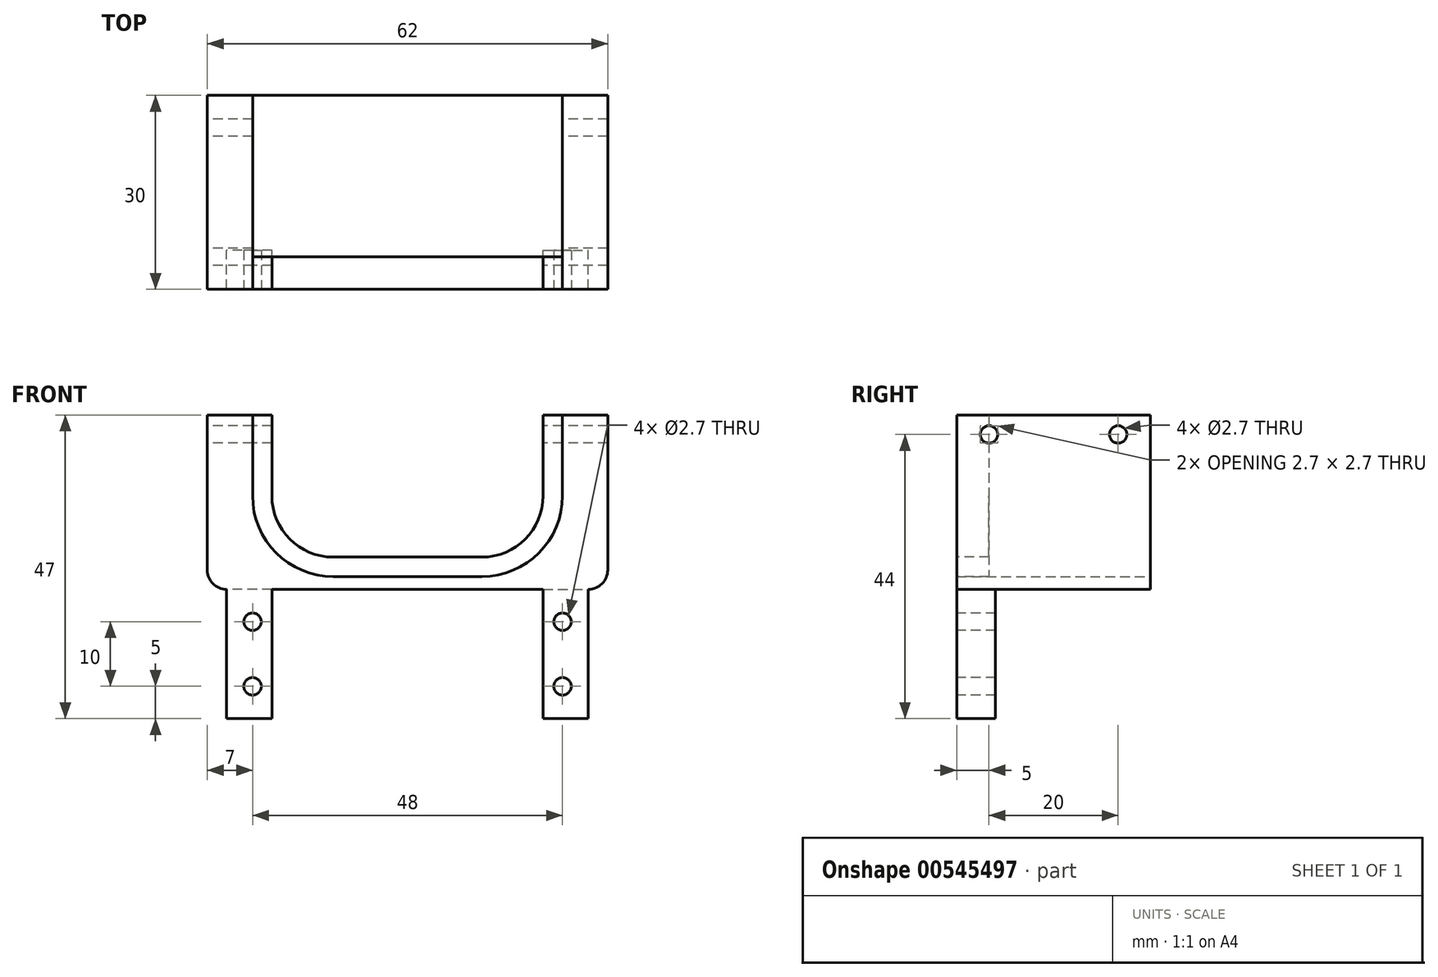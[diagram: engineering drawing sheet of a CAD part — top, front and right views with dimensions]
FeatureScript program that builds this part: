
annotation { "Feature Type Name" : "Feature", "Feature Type Description" : "" }
export const myFeature = defineFeature(function(context is Context, id is Id, definition is map)
    precondition{}
    {
        {
            var Q0;
            Q0=qCreatedBy(makeId("Front.planeOp"),FACE);
            var sketch = newSketch(context, id + "F0", { "sketchPlane" : qUnion([Q0])});
            skLineSegment(sketch, "E0.bottom", {"start": v(31, -13.5) * mm, "end": v(-31, -13.5) * mm});
            skLineSegment(sketch, "E0.top", {"start": v(31, 13.5) * mm, "end": v(-31, 13.5) * mm});
            skLineSegment(sketch, "E0.left", {"start": v(31, -13.5) * mm, "end": v(31, 13.5) * mm});
            skLineSegment(sketch, "E0.right", {"start": v(-31, -13.5) * mm, "end": v(-31, 13.5) * mm});
            skPoint(sketch, "E0.middle", {"position": v(0, 0) * mm});
            skLineSegment(sketch, "E1", {"start": v(24, 13.5) * mm, "end": v(24, 1) * mm});
            skLineSegment(sketch, "E2.MirrorCS", {"start": v(-24, 13.5) * mm, "end": v(-24, 1) * mm});
            skLineSegment(sketch, "E3", {"start": v(-11.5, -11.5) * mm, "end": v(11.5, -11.5) * mm});
            skPoint(sketch, "E4.orphan", {"position": v(24, -13.5) * mm});
            skPoint(sketch, "E5.orphan", {"position": v(-24, -13.5) * mm});
            skPoint(sketch, "E6.visualSharp", {"position": v(-24, -11.5) * mm});
            skArc(sketch, "E6.filletArc", {"start": v(-24, 1) * mm, "mid": v(-20.34, -7.84) * mm, "end": v(-11.5, -11.5) * mm});
            skPoint(sketch, "E7.visualSharp", {"position": v(24, -11.5) * mm});
            skArc(sketch, "E7.filletArc", {"start": v(11.5, -11.5) * mm, "mid": v(20.34, -7.84) * mm, "end": v(24, 1) * mm});
            skLineSegment(sketch, "E8.0", {"start": v(-19, 13.5) * mm, "end": v(-19, 1) * mm});
            skLineSegment(sketch, "E9.0", {"start": v(19, 13.5) * mm, "end": v(19, 1) * mm});
            skArc(sketch, "E9.1", {"start": v(11.5, -6.5) * mm, "mid": v(16.8, -4.3) * mm, "end": v(19, 1) * mm});
            skLineSegment(sketch, "E9.2", {"start": v(-11.5, -6.5) * mm, "end": v(11.5, -6.5) * mm});
            skArc(sketch, "E9.3", {"start": v(-19, 1) * mm, "mid": v(-16.8, -4.3) * mm, "end": v(-11.5, -6.5) * mm});
            skSolve(sketch);
        }
        {
            var Q0;
            Q0=makeQuery(id+"F0.imprint","IMPRINT",FACE,{"disambiguationData":[TD([[makeQuery(id+"F0.imprint","IMPRINT",EDGE,{"derivedFrom":sQuery(id+"F0.wireOp",EDGE,"E0.bottom")}),-1.0]])]});
            extrude(context, id + "F1", {"entities" : qUnion([Q0]), "depth" : 30 * mm, "offsetDistance" : 25 * mm});
        }
        {
            var Q0;
            Q0=makeQuery(id+"F1.opExtrude","SWEPT_FACE",FACE,{"disambiguationData":[OSD([sQuery(id+"F0.wireOp",EDGE,"E0.bottom")])]});
            var sketch = newSketch(context, id + "F2", { "sketchPlane" : qUnion([Q0])});
            skLineSegment(sketch, "E10.bottom", {"start": v(31, 0) * mm, "end": v(-31, 0) * mm});
            skLineSegment(sketch, "E10.top", {"start": v(31, 3) * mm, "end": v(-31, 3) * mm});
            skLineSegment(sketch, "E10.left", {"start": v(31, 0) * mm, "end": v(31, 3) * mm});
            skLineSegment(sketch, "E10.right", {"start": v(-31, 0) * mm, "end": v(-31, 3) * mm});
            skSolve(sketch);
        }
        {
            var Q0;
            Q0=makeQuery(id+"F1.opExtrude","CAP_FACE",FACE,{"disambiguationData":[OSD([sQuery(id+"F0.wireOp",EDGE,"E0.bottom"),sQuery(id+"F0.wireOp",EDGE,"E0.top"),sQuery(id+"F0.wireOp",EDGE,"E0.left"),sQuery(id+"F0.wireOp",EDGE,"E0.right"),sQuery(id+"F0.wireOp",EDGE,"E1"),sQuery(id+"F0.wireOp",EDGE,"E2.MirrorCS"),sQuery(id+"F0.wireOp",EDGE,"E3"),sQuery(id+"F0.wireOp",EDGE,"E6.filletArc"),sQuery(id+"F0.wireOp",EDGE,"E7.filletArc")])],"isStart":false});
            var sketch = newSketch(context, id + "F3", { "sketchPlane" : qUnion([Q0])});
            skArc(sketch, "E11.0", {"start": v(-21, 1) * mm, "mid": v(-18.22, -5.72) * mm, "end": v(-11.5, -8.5) * mm});
            skLineSegment(sketch, "E12.0", {"start": v(-21, 13.5) * mm, "end": v(-21, 1) * mm});
            skLineSegment(sketch, "E13.0", {"start": v(-11.5, -8.5) * mm, "end": v(11.5, -8.5) * mm});
            skArc(sketch, "E14.0", {"start": v(11.5, -8.5) * mm, "mid": v(18.22, -5.72) * mm, "end": v(21, 1) * mm});
            skLineSegment(sketch, "E15.0", {"start": v(21, 13.5) * mm, "end": v(21, 1) * mm});
            skLineSegment(sketch, "E16", {"start": v(21, 13.5) * mm, "end": v(24, 13.5) * mm});
            skLineSegment(sketch, "E17", {"start": v(-21, 13.5) * mm, "end": v(-24, 13.5) * mm});
            skSolve(sketch);
        }
        {
            var Q0;
            Q0=makeQuery(id+"F3.imprint","IMPRINT",FACE,{"disambiguationData":[TD([[makeQuery(id+"F3.imprint","IMPRINT",EDGE,{"derivedFrom":sQuery(id+"F3.wireOp",EDGE,"E11.0")}),-1.0]])]});
            extrude(context, id + "F4", {"entities" : qUnion([Q0]), "oppositeDirection" : true, "depth" : 5 * mm, "offsetDistance" : 25 * mm});
        }
        {
            var Q0;
            Q0=makeQuery(id+"F1.opExtrude","SWEPT_FACE",FACE,{"disambiguationData":[OSD([sQuery(id+"F0.wireOp",EDGE,"E0.right")])]});
            var sketch = newSketch(context, id + "F5", { "sketchPlane" : qUnion([Q0])});
            skCircle(sketch, "E18", {"center": v(25, 10.5) * mm, "radius": 1.35 * mm});
            skCircle(sketch, "E19", {"center": v(5, 10.5) * mm, "radius": 1.35 * mm});
            skSolve(sketch);
        }
        {
            var Q0;
            Q0=makeQuery(id+"F5.imprint","IMPRINT",FACE,{"disambiguationData":[TD([[makeQuery(id+"F5.imprint","IMPRINT",EDGE,{"derivedFrom":sQuery(id+"F5.wireOp",EDGE,"E18")}),1.0]])]});
            var Q1;
            Q1=makeQuery(id+"F5.imprint","IMPRINT",FACE,{"disambiguationData":[TD([[makeQuery(id+"F5.imprint","IMPRINT",EDGE,{"derivedFrom":sQuery(id+"F5.wireOp",EDGE,"E19")}),1.0]])]});
            extrude(context, id + "F6", {"entities" : qUnion([Q0, Q1]), "operationType" : NewBodyOperationType.REMOVE, "endBound" : BoundingType.THROUGH_ALL, "oppositeDirection" : true, "depth" : 25 * mm, "offsetDistance" : 25 * mm});
        }
        {
            var Q0;
            {var subQ0=sQuery(id+"F2.wireOp",EDGE,"E10.top");Q0=makeQuery(id+"F2.imprint","IMPRINT",FACE,{"disambiguationData":[TD([[makeQuery(id+"F2.imprint","IMPRINT",EDGE,{"derivedFrom":subQ0}),-1.0]])]});}
            var sketch = newSketch(context, id + "F7", { "sketchPlane" : qUnion([Q0])});
            skLineSegment(sketch, "E20.bottom", {"start": v(21, 30) * mm, "end": v(28, 30) * mm});
            skLineSegment(sketch, "E20.top", {"start": v(21, 24) * mm, "end": v(28, 24) * mm});
            skLineSegment(sketch, "E20.left", {"start": v(21, 30) * mm, "end": v(21, 24) * mm});
            skLineSegment(sketch, "E20.right", {"start": v(28, 30) * mm, "end": v(28, 24) * mm});
            skLineSegment(sketch, "E21.MirrorCS", {"start": v(-21, 30) * mm, "end": v(-21, 24) * mm});
            skLineSegment(sketch, "E22.MirrorCS", {"start": v(-21, 24) * mm, "end": v(-28, 24) * mm});
            skLineSegment(sketch, "E23.MirrorCS", {"start": v(-28, 30) * mm, "end": v(-28, 24) * mm});
            skLineSegment(sketch, "E24.MirrorCS", {"start": v(-21, 30) * mm, "end": v(-28, 30) * mm});
            skSolve(sketch);
        }
        {
            var Q0;
            Q0=makeQuery(id+"F7.imprint","IMPRINT",FACE,{"disambiguationData":[TD([[makeQuery(id+"F7.imprint","IMPRINT",EDGE,{"derivedFrom":sQuery(id+"F7.wireOp",EDGE,"E21.MirrorCS")}),-1.0]])]});
            var Q1;
            Q1=makeQuery(id+"F7.imprint","IMPRINT",FACE,{"disambiguationData":[TD([[makeQuery(id+"F7.imprint","IMPRINT",EDGE,{"derivedFrom":sQuery(id+"F7.wireOp",EDGE,"E20.bottom")}),1.0]])]});
            extrude(context, id + "F8", {"entities" : qUnion([Q0, Q1]), "operationType" : NewBodyOperationType.ADD, "depth" : 20 * mm, "offsetDistance" : 25 * mm});
        }
        {
            var Q0;
            Q0=makeQuery(id+"F8.boolean.opBoolean","MERGE",FACE,{"derivedFrom":[makeQuery(id+"F1.opExtrude","CAP_FACE",FACE,{"disambiguationData":[OSD([sQuery(id+"F0.wireOp",EDGE,"E0.bottom"),sQuery(id+"F0.wireOp",EDGE,"E0.top"),sQuery(id+"F0.wireOp",EDGE,"E0.left"),sQuery(id+"F0.wireOp",EDGE,"E0.right"),sQuery(id+"F0.wireOp",EDGE,"E1"),sQuery(id+"F0.wireOp",EDGE,"E2.MirrorCS"),sQuery(id+"F0.wireOp",EDGE,"E3"),sQuery(id+"F0.wireOp",EDGE,"E6.filletArc"),sQuery(id+"F0.wireOp",EDGE,"E7.filletArc")])],"isStart":false}),makeQuery(id+"F8.opExtrude","SWEPT_FACE",FACE,{"disambiguationData":[OSD([sQuery(id+"F7.wireOp",EDGE,"E20.bottom")])]}),makeQuery(id+"F8.opExtrude","SWEPT_FACE",FACE,{"disambiguationData":[OSD([sQuery(id+"F7.wireOp",EDGE,"E24.MirrorCS")])]})]});
            var sketch = newSketch(context, id + "F9", { "sketchPlane" : qUnion([Q0])});
            skLineSegment(sketch, "E25", {"start": v(-28, -13.5) * mm, "end": v(-21, -13.5) * mm});
            skLineSegment(sketch, "E26", {"start": v(21, -13.5) * mm, "end": v(28, -13.5) * mm});
            skSolve(sketch);
        }
        {
            var Q0;
            Q0=makeQuery(id+"F9.imprint","IMPRINT",FACE,{"disambiguationData":[TD([[makeQuery(id+"F9.imprint","IMPRINT",EDGE,{"derivedFrom":sQuery(id+"F9.wireOp",EDGE,"E25")}),-1.0]])]});
            var sketch = newSketch(context, id + "F10", { "sketchPlane" : qUnion([Q0])});
            skCircle(sketch, "E27", {"center": v(-24, -18.5) * mm, "radius": 1.35 * mm});
            skCircle(sketch, "E28", {"center": v(24, -18.5) * mm, "radius": 1.35 * mm});
            skCircle(sketch, "E29", {"center": v(24, -28.5) * mm, "radius": 1.35 * mm});
            skCircle(sketch, "E30", {"center": v(-24, -28.5) * mm, "radius": 1.35 * mm});
            skSolve(sketch);
        }
        {
            var Q0;
            Q0=makeQuery(id+"F10.imprint","IMPRINT",FACE,{"disambiguationData":[TD([[makeQuery(id+"F10.imprint","IMPRINT",EDGE,{"derivedFrom":sQuery(id+"F10.wireOp",EDGE,"E27")}),1.0]])]});
            var Q1;
            Q1=makeQuery(id+"F10.imprint","IMPRINT",FACE,{"disambiguationData":[TD([[makeQuery(id+"F10.imprint","IMPRINT",EDGE,{"derivedFrom":sQuery(id+"F10.wireOp",EDGE,"E30")}),1.0]])]});
            var Q2;
            Q2=makeQuery(id+"F10.imprint","IMPRINT",FACE,{"disambiguationData":[TD([[makeQuery(id+"F10.imprint","IMPRINT",EDGE,{"derivedFrom":sQuery(id+"F10.wireOp",EDGE,"E28")}),1.0]])]});
            var Q3;
            Q3=makeQuery(id+"F10.imprint","IMPRINT",FACE,{"disambiguationData":[TD([[makeQuery(id+"F10.imprint","IMPRINT",EDGE,{"derivedFrom":sQuery(id+"F10.wireOp",EDGE,"E29")}),1.0]])]});
            extrude(context, id + "F11", {"entities" : qUnion([Q0, Q1, Q2, Q3]), "operationType" : NewBodyOperationType.REMOVE, "endBound" : BoundingType.THROUGH_ALL, "oppositeDirection" : true, "depth" : 25 * mm, "offsetDistance" : 25 * mm});
        }
        {
            var Q0;
            Q0=makeQuery(id+"F1.opExtrude","SWEPT_EDGE",EDGE,{"disambiguationData":[OSD([sQuery(id+"F0.wireOp",EDGE,"E0.bottom"),sQuery(id+"F0.wireOp",EDGE,"E0.right")])]});
            var Q1;
            Q1=makeQuery(id+"F1.opExtrude","SWEPT_EDGE",EDGE,{"disambiguationData":[OSD([sQuery(id+"F0.wireOp",EDGE,"E0.bottom"),sQuery(id+"F0.wireOp",EDGE,"E0.left")])]});
            fillet(context, id + "F12", {"entities" : qUnion([Q0, Q1]), "radius" : 3 * mm, "tangentPropagation" : true, "allowEdgeOverflow" : false});
        }
    });
